# Revit family: Lighting-Spot-LSI_LX2030 (1)
name_source: partatom
category: Lighting Fixtures
revit_build: Autodesk Revit MEP 2012 (Build: 20110309_2315(x64)
units: mm (PartAtom-declared; Revit-internal decimal feet)

## types (1)
- Load Type Catalog
    Apparent Load = 0 VA
    Color Filter = 16777215
    Default Elevation = 2"
    Description = Spot Light
    Dimming Lamp Color Temperature Shift = <None>
    Emit Shape Visible in Rendering = No
    Emit from Circle Diameter = 2 1/4"
    IES File Link = http://www.lightingservicesinc.com
    Lumens/CRI/Wattage = Load Type Catalog
    Manufacturer = Lighting Services Inc
    Material = Paint - LSI - White
    Model = Load Type Catalog
    Number of Poles = 1
    OmniClass Number = 23.35.47.11.11.19
    OmniClass Title = Non Weather Rated Light Emitting Diode Lighting Fixtures
    Photometric Web File = L238591-2.IES
    Power Factor = 1
    Product Documentation Link = http://www.lightingservicesinc.com
    Reflector = 54mm 40°
    Tilt Angle = 90.00°
    URL = http://www.lightingservicesinc.com
    Voltage = 120 V

## geometry (parser evidence)
native form markers: Blend x8, Sweep x3
no freeform markers — native parametric forms only
